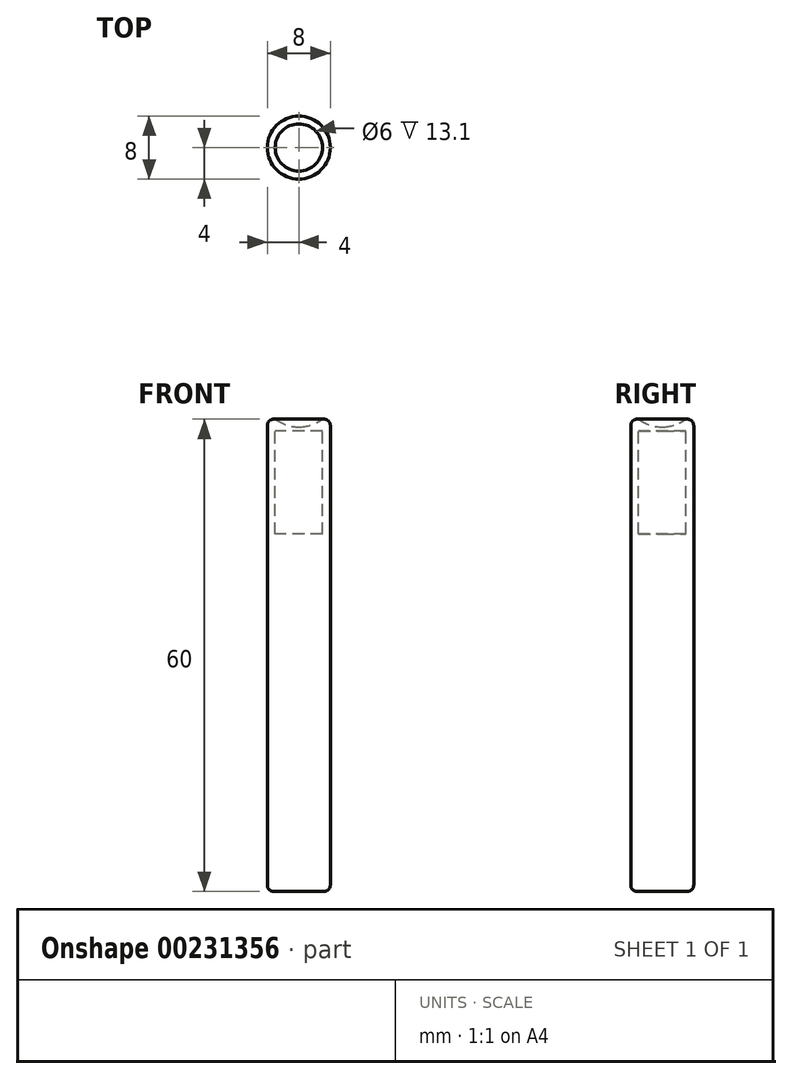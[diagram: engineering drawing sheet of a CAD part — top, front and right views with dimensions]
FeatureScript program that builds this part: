
annotation { "Feature Type Name" : "Feature", "Feature Type Description" : "" }
export const myFeature = defineFeature(function(context is Context, id is Id, definition is map)
    precondition{}
    {
        {
            var Q0;
            Q0=qCreatedBy(makeId("Top.planeOp"),FACE);
            var sketch = newSketch(context, id + "F0", { "sketchPlane" : qUnion([Q0])});
            skCircle(sketch, "E0", {"center": v(0, 0) * mm, "radius": 4 * mm});
            skSolve(sketch);
        }
        {
            var Q0;
            Q0 = qSketchRegion(id + "F0", true);
            extrude(context, id + "F1", {"entities" : qUnion([Q0]), "depth" : 30 * mm, "hasSecondDirection" : true, "secondDirectionOppositeDirection" : true, "secondDirectionDepth" : 30 * mm});
        }
        {
            var Q0;
            Q0=qCreatedBy(makeId("Front.planeOp"),FACE);
            var sketch = newSketch(context, id + "F2", { "sketchPlane" : qUnion([Q0])});
            skLineSegment(sketch, "E1", {"start": v(0, 0) * mm, "end": v(0, 34) * mm});
            skCircle(sketch, "E2", {"center": v(0, 34) * mm, "radius": 5 * mm});
            skLineSegment(sketch, "E3", {"start": v(0, 39) * mm, "end": v(0, 34) * mm});
            skSolve(sketch);
        }
        {
            var Q0;
            {var subQ0=sQuery(id+"F2.wireOp",EDGE,"E3");Q0=makeQuery(id+"F2.imprint","IMPRINT",FACE,{"disambiguationData":[TD([[makeQuery(id+"F2.imprint","IMPRINT",EDGE,{"derivedFrom":subQ0}),1.0]])]});}
            var Q1;
            Q1=sQuery(id+"F2.wireOp",EDGE,"E3");
            revolve(context, id + "F3", {"operationType" : NewBodyOperationType.REMOVE, "entities" : qUnion([Q0]), "axis" : qUnion([Q1]), "revolveType" : RevolveType.FULL, "oppositeDirection" : true});
        }
        {
            var Q0;
            Q0=makeQuery(id+"F1.opExtrude","CAP_EDGE",EDGE,{"disambiguationData":[OSD([sQuery(id+"F0.wireOp",EDGE,"E0")])],"isStart":false});
            var Q1;
            Q1=makeQuery(id+"F1.opExtrude","CAP_EDGE",EDGE,{"disambiguationData":[OSD([sQuery(id+"F0.wireOp",EDGE,"E0")])],"isStart":true});
            fillet(context, id + "F4", {"entities" : qUnion([Q0, Q1]), "radius" : 0.8 * mm, "tangentPropagation" : true, "allowEdgeOverflow" : false});
        }
        {
            var Q0;
            Q0=makeQuery(id+"F1.opExtrude","CAP_FACE",FACE,{"disambiguationData":[OSD([sQuery(id+"F0.wireOp",EDGE,"E0")])],"isStart":false});
            var sketch = newSketch(context, id + "F5", { "sketchPlane" : qUnion([Q0])});
            skCircle(sketch, "E4", {"center": v(0, 0) * mm, "radius": 3 * mm});
            skSolve(sketch);
        }
        {
            var Q0;
            Q0 = qSketchRegion(id + "F5", true);
            extrude(context, id + "F6", {"entities" : qUnion([Q0]), "operationType" : NewBodyOperationType.REMOVE, "oppositeDirection" : true, "depth" : 14.6 * mm, "hasSecondDirection" : true, "secondDirectionOppositeDirection" : true, "secondDirectionDepth" : 1.5 * mm});
        }
    });
